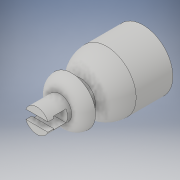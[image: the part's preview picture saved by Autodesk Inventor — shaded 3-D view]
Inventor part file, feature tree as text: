
AUTODESK INVENTOR PART (.ipt)
format: ipt  version: 2018 (Build 220112000, 112)  size: 196,096 bytes
history: native  units: mm
features: extrude x10, sketch x10, fillet x2
ambient origin geometry x8: Origin, YZ Plane, XZ Plane, XY Plane, X Axis, Y Axis, Z Axis, Center Point
bodies: Volumenkörper1 (feature_tree), Volumenkörper2 (feature_tree)
feature tree (22):
  extrude  "Extrusion1"  Depth=2.0mm TaperAngle=0.0deg
  fillet  "Rundung1"  Radius=2.0mm
  extrude  "Extrusion2"  Depth=1.5mm TaperAngle=0.0deg
  extrude  "Extrusion3"  Depth=10.0mm TaperAngle=0.0deg
  extrude  "Extrusion5"  Depth=2.5mm TaperAngle=0.0deg
  extrude  "Extrusion6"  Depth=2.5mm TaperAngle=0.0deg
  extrude  "Extrusion7"  Depth=1.6mm TaperAngle=0.0deg
  fillet  "Rundung2"  Radius=5.0mm
  extrude  "Extrusion10"  Depth=4.85mm TaperAngle=0.0deg
  extrude  "Extrusion11"  Depth=2.15mm TaperAngle=0.0deg
  extrude  "Extrusion12"  Depth=1.0mm TaperAngle=0.0deg
  extrude  "Extrusion14"  Depth=1.0mm
  sketch  "Skizze1"  dims[d0=8.0mm d1=2.0mm d2=0.0mm d3=2.0mm]
  sketch  "Skizze2"  dims[d4=5.0mm d5=1.5mm d6=0.0mm]
  sketch  "Skizze3"  dims[d7=10.0mm d8=8.0mm d9=0.0mm]
  sketch  "Skizze5"  dims[d13=10.0mm d14=2.5mm d15=0.0mm]
  sketch  "Skizze6"  dims[d16=8.5mm d17=2.5mm d18=0.0mm]
  sketch  "Skizze8"  dims[d19=1.6mm d20=1.6mm d21=0.0mm d22=5.0mm]
  sketch  "Skizze11"  dims[d23=4.0mm d28=4.85mm d29=0.0mm]
  sketch  "Skizze15"  dims[d30=2.0mm d31=2.15mm d32=0.0mm]
  sketch  "Skizze16"  dims[d33=4.0mm d34=1.0mm d35=0.0mm]
  sketch  "Skizze18"  dims[d38=1.0mm d39=0.0mm d26=1.0mm d27=1.0mm]
